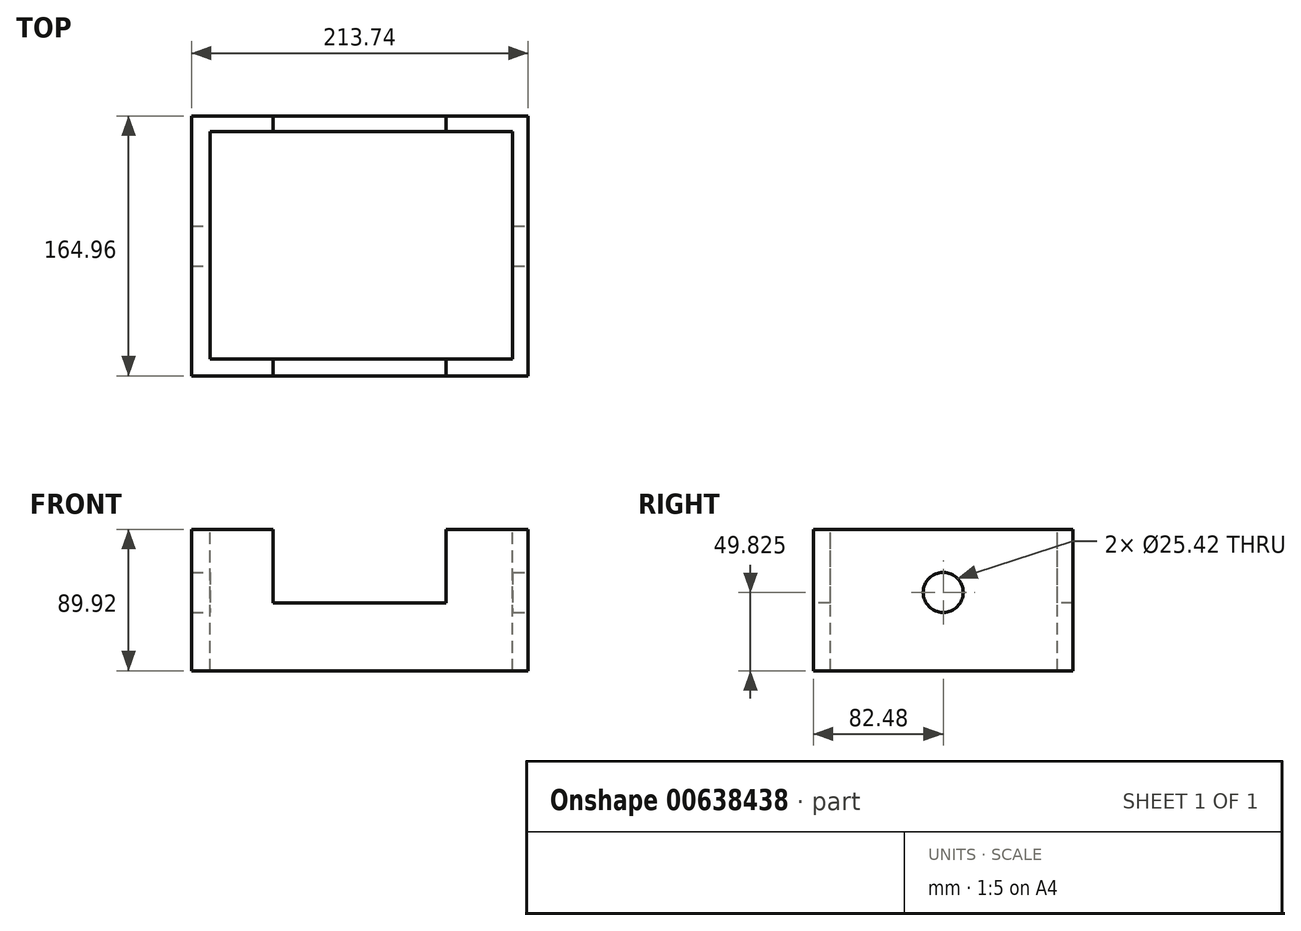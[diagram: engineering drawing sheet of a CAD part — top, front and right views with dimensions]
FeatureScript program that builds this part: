
annotation { "Feature Type Name" : "Feature", "Feature Type Description" : "" }
export const myFeature = defineFeature(function(context is Context, id is Id, definition is map)
    precondition{}
    {
        {
            var Q0;
            Q0=qCreatedBy(makeId("Top.planeOp"),FACE);
            var sketch = newSketch(context, id + "F0", { "sketchPlane" : qUnion([Q0])});
            skLineSegment(sketch, "E0.bottom", {"start": v(-106.87, -82.48) * mm, "end": v(106.87, -82.48) * mm});
            skLineSegment(sketch, "E0.top", {"start": v(-106.87, 82.48) * mm, "end": v(106.87, 82.48) * mm});
            skLineSegment(sketch, "E0.left", {"start": v(-106.87, -82.48) * mm, "end": v(-106.87, 82.48) * mm});
            skLineSegment(sketch, "E0.right", {"start": v(106.87, -82.48) * mm, "end": v(106.87, 82.48) * mm});
            skPoint(sketch, "E0.middle", {"position": v(0, 0) * mm});
            skSolve(sketch);
        }
        {
            var Q0;
            Q0=makeQuery(id+"F0.imprint","IMPRINT",FACE,{"disambiguationData":[TD([[makeQuery(id+"F0.imprint","IMPRINT",EDGE,{"derivedFrom":sQuery(id+"F0.wireOp",EDGE,"E0.bottom")}),1.0]])]});
            extrude(context, id + "F1", {"entities" : qUnion([Q0]), "depth" : 89.92 * mm, "offsetDistance" : 25.4 * mm});
        }
        {
            var Q0;
            Q0=makeQuery(id+"F1.opExtrude","CAP_FACE",FACE,{"disambiguationData":[OSD([sQuery(id+"F0.wireOp",EDGE,"E0.bottom"),sQuery(id+"F0.wireOp",EDGE,"E0.top"),sQuery(id+"F0.wireOp",EDGE,"E0.left"),sQuery(id+"F0.wireOp",EDGE,"E0.right")])],"isStart":false});
            var sketch = newSketch(context, id + "F2", { "sketchPlane" : qUnion([Q0])});
            skLineSegment(sketch, "E1.bottom", {"start": v(-95.1, 72.5) * mm, "end": v(97.13, 72.5) * mm});
            skLineSegment(sketch, "E1.top", {"start": v(-95.1, -71.69) * mm, "end": v(97.13, -71.69) * mm});
            skLineSegment(sketch, "E1.left", {"start": v(-95.1, 72.5) * mm, "end": v(-95.1, -71.69) * mm});
            skLineSegment(sketch, "E1.right", {"start": v(97.13, 72.5) * mm, "end": v(97.13, -71.69) * mm});
            skSolve(sketch);
        }
        {
            var Q0;
            Q0=makeQuery(id+"F2.imprint","IMPRINT",FACE,{"disambiguationData":[TD([[makeQuery(id+"F2.imprint","IMPRINT",EDGE,{"derivedFrom":sQuery(id+"F2.wireOp",EDGE,"E1.bottom")}),-1.0]])]});
            extrude(context, id + "F3", {"entities" : qUnion([Q0]), "operationType" : NewBodyOperationType.REMOVE, "oppositeDirection" : true, "depth" : 137.67 * mm, "offsetDistance" : 25.4 * mm});
        }
        {
            var Q0;
            Q0=makeQuery(id+"F1.opExtrude","SWEPT_FACE",FACE,{"disambiguationData":[OSD([sQuery(id+"F0.wireOp",EDGE,"E0.bottom")])]});
            var sketch = newSketch(context, id + "F4", { "sketchPlane" : qUnion([Q0])});
            skLineSegment(sketch, "E2.bottom", {"start": v(-54.95, 43.03) * mm, "end": v(54.95, 43.03) * mm});
            skLineSegment(sketch, "E2.left", {"start": v(-54.95, 43.03) * mm, "end": v(-54.95, 89.92) * mm});
            skLineSegment(sketch, "E2.right", {"start": v(54.95, 43.03) * mm, "end": v(54.95, 89.92) * mm});
            skPoint(sketch, "E2.middle", {"position": v(0, 89.92) * mm});
            skLineSegment(sketch, "E3", {"start": v(-54.95, 89.92) * mm, "end": v(54.95, 89.92) * mm});
            skPoint(sketch, "E2.top.start.orphan", {"position": v(-54.95, 136.8) * mm});
            skPoint(sketch, "E4.orphan", {"position": v(54.95, 136.8) * mm});
            skSolve(sketch);
        }
        {
            var Q0;
            Q0=makeQuery(id+"F4.imprint","IMPRINT",FACE,{"disambiguationData":[TD([[makeQuery(id+"F4.imprint","IMPRINT",EDGE,{"derivedFrom":sQuery(id+"F4.wireOp",EDGE,"E2.bottom")}),1.0]])]});
            extrude(context, id + "F5", {"entities" : qUnion([Q0]), "operationType" : NewBodyOperationType.REMOVE, "oppositeDirection" : true, "depth" : 190.25 * mm, "offsetDistance" : 25.4 * mm});
        }
        {
            var Q0;
            Q0=makeQuery(id+"F1.opExtrude","SWEPT_FACE",FACE,{"disambiguationData":[OSD([sQuery(id+"F0.wireOp",EDGE,"E0.right")])]});
            var sketch = newSketch(context, id + "F6", { "sketchPlane" : qUnion([Q0])});
            skCircle(sketch, "E5", {"center": v(0, 49.82) * mm, "radius": 12.7 * mm});
            skSolve(sketch);
        }
        {
            var Q0;
            Q0=makeQuery(id+"F6.imprint","IMPRINT",FACE,{"disambiguationData":[TD([[makeQuery(id+"F6.imprint","IMPRINT",EDGE,{"derivedFrom":sQuery(id+"F6.wireOp",EDGE,"E5")}),1.0]])]});
            extrude(context, id + "F7", {"entities" : qUnion([Q0]), "operationType" : NewBodyOperationType.REMOVE, "oppositeDirection" : true, "depth" : 299.2 * mm, "offsetDistance" : 25.4 * mm});
        }
    });
